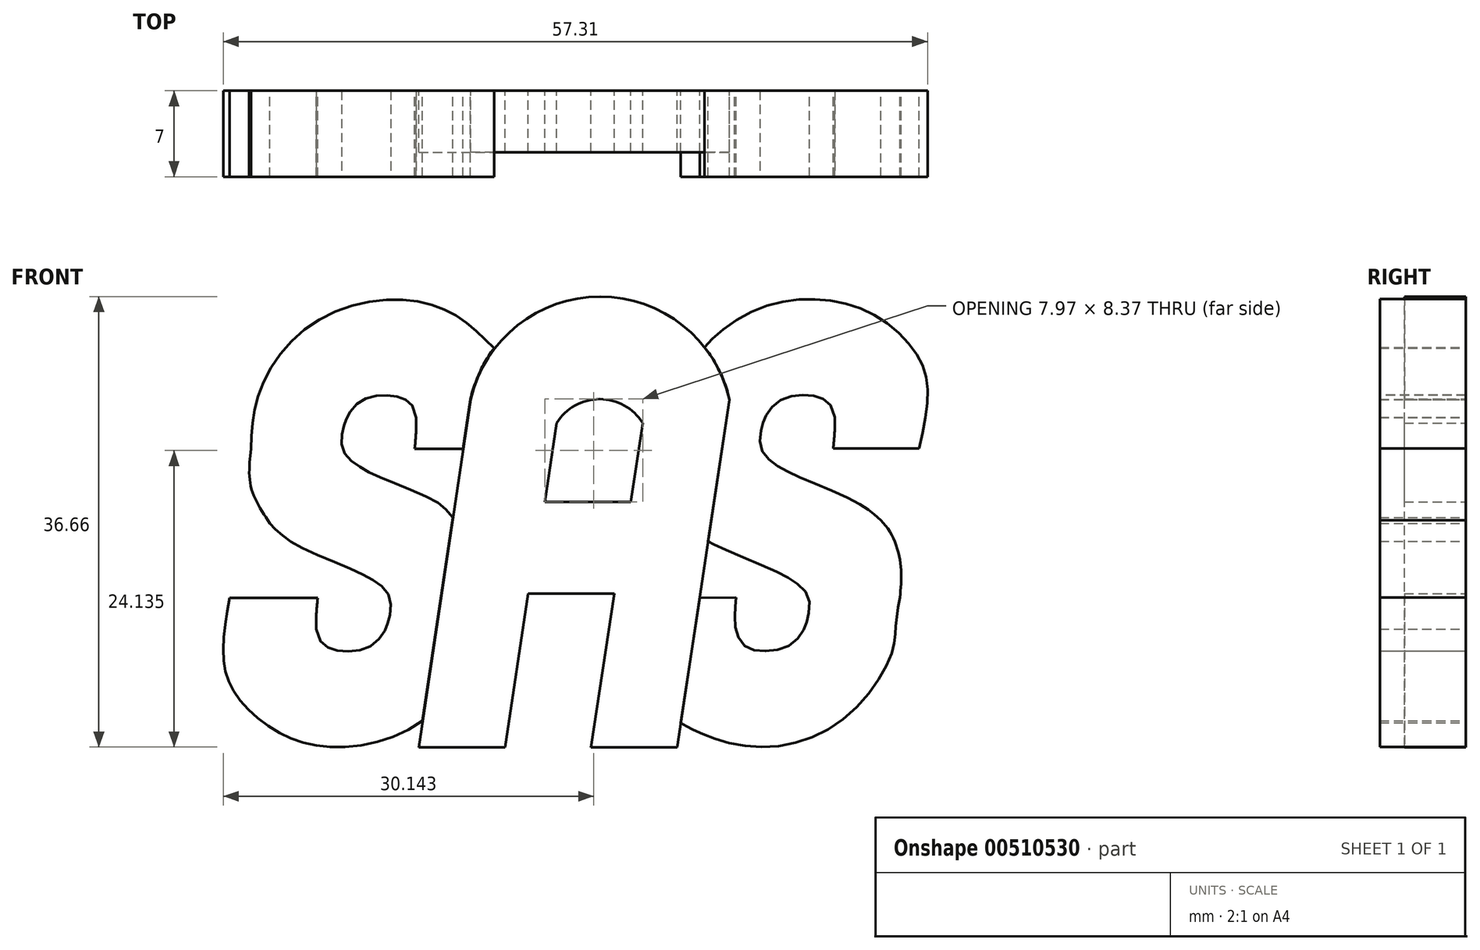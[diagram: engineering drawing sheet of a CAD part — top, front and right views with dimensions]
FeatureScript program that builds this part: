
annotation { "Feature Type Name" : "Feature", "Feature Type Description" : "" }
export const myFeature = defineFeature(function(context is Context, id is Id, definition is map)
    precondition{}
    {
        {
            var Q0;
            Q0=qCreatedBy(makeId("Front.planeOp"),FACE);
            var sketch = newSketch(context, id + "F0", { "sketchPlane" : qUnion([Q0])});
            skLineSegment(sketch, "E0", {"start": v(7, 0) * mm, "end": v(14, 0) * mm});
            skLineSegment(sketch, "E1", {"start": v(28, 0) * mm, "end": v(21, 0) * mm});
            skLineSegment(sketch, "E2", {"start": v(21, 0) * mm, "end": v(22.89, 12.5) * mm});
            skLineSegment(sketch, "E3", {"start": v(22.89, 12.5) * mm, "end": v(15.89, 12.48) * mm});
            skLineSegment(sketch, "E4", {"start": v(15.89, 12.48) * mm, "end": v(14, 0) * mm});
            skLineSegment(sketch, "E5", {"start": v(17.24, 19.95) * mm, "end": v(24.24, 19.95) * mm});
            skLineSegment(sketch, "E6", {"start": v(24.24, 19.95) * mm, "end": v(25.2, 26.38) * mm});
            skLineSegment(sketch, "E7", {"start": v(17.24, 19.95) * mm, "end": v(18.2, 26.38) * mm});
            skLineSegment(sketch, "E8", {"start": v(17.24, 19.95) * mm, "end": v(20.74, 19.95) * mm, "construction": true});
            skPoint(sketch, "E9.endSnap0", {"position": v(21.7, 28.32) * mm});
            skLineSegment(sketch, "E10", {"start": v(28, 0) * mm, "end": v(32.27, 28.28) * mm});
            skLineSegment(sketch, "E11", {"start": v(7, 0) * mm, "end": v(11.21, 28.31) * mm});
            skArc(sketch, "E12", {"start": v(32.27, 28.28) * mm, "mid": v(21.75, 36.66) * mm, "end": v(11.21, 28.31) * mm});
            skArc(sketch, "E13", {"start": v(25.2, 26.38) * mm, "mid": v(21.7, 28.32) * mm, "end": v(18.2, 26.38) * mm});
            skSolve(sketch);
        }
        {
            var Q0;
            Q0=qCreatedBy(makeId("Front.planeOp"),FACE);
            var sketch = newSketch(context, id + "F1", { "sketchPlane" : qUnion([Q0])});
            skLineSegment(sketch, "E14", {"start": v(0, 0) * mm, "end": v(-10.16, 0) * mm, "construction": true});
            skLineSegment(sketch, "E15", {"start": v(0, 0) * mm, "end": v(10.14, 0) * mm, "construction": true});
            skFitSpline(sketch, "E16", {"points": [v(-6.66, 24.28) * mm, v(-6.66, 21.15) * mm, v(-5.12, 18.2) * mm], "startDerivative": vector(-0.75, -6.48) * mm, "endDerivative": vector(3.8, -5.67) * mm});
            skLineSegment(sketch, "E17", {"start": v(6.66, 24.28) * mm, "end": v(0.78, 24.28) * mm, "construction": true});
            skFitSpline(sketch, "E18", {"points": [v(6.78, 26.82) * mm, v(5.8, 28.32) * mm, v(4.13, 28.62) * mm, v(2.18, 28.1) * mm, v(1.14, 26.82) * mm, v(0.84, 25.93) * mm, v(0.78, 24.28) * mm, v(1.93, 22.98) * mm, v(4, 21.9) * mm, v(8.24, 20.05) * mm, v(9.75, 18.67) * mm], "startDerivative": vector(-4.4, 29.75) * mm, "endDerivative": vector(12.93, -18.47) * mm});
            skFitSpline(sketch, "E19", {"points": [v(6.66, 24.28) * mm, v(6.76, 25.47) * mm, v(6.78, 26.82) * mm], "startDerivative": vector(0.34, 3.42) * mm, "endDerivative": vector(-0.13, 3.63) * mm});
            skFitSpline(sketch, "E20.MirrorCS", {"points": [v(-1.36, 9.6) * mm, v(-0.38, 8.09) * mm, v(1.3, 7.8) * mm, v(3.24, 8.32) * mm, v(4.28, 9.6) * mm, v(4.58, 10.49) * mm, v(4.64, 12.14) * mm, v(3.5, 13.44) * mm, v(1.41, 14.52) * mm, v(-2.82, 16.37) * mm, v(-4.28, 17.38) * mm, v(-5.12, 18.2) * mm], "startDerivative": vector(4.4, -29.75) * mm, "endDerivative": vector(-6, 10.66) * mm});
            skFitSpline(sketch, "E21.MirrorCS", {"points": [v(-1.23, 12.14) * mm, v(-1.34, 10.94) * mm, v(-1.36, 9.6) * mm], "startDerivative": vector(-0.34, -3.42) * mm, "endDerivative": vector(0.13, -3.63) * mm});
            skFitSpline(sketch, "E22", {"points": [v(-8.41, 12.14) * mm, v(-8.91, 7.45) * mm, v(-7.96, 4.37) * mm, v(-4.65, 1.34) * mm, v(0.17, 0) * mm, v(7.3, 2.15) * mm], "startDerivative": vector(-4.29, -25.2) * mm, "endDerivative": vector(25.16, 18.75) * mm});
            skLineSegment(sketch, "E23", {"start": v(9.75, 18.67) * mm, "end": v(7.3, 2.15) * mm});
            skLineSegment(sketch, "E24", {"start": v(6.66, 24.28) * mm, "end": v(10.6, 24.27) * mm});
            skFitSpline(sketch, "E25", {"points": [v(-6.66, 24.28) * mm, v(-6.02, 28.74) * mm, v(-1.96, 34.25) * mm, v(5.25, 36.41) * mm, v(10.08, 35.08) * mm, v(13.12, 32.45) * mm], "startDerivative": vector(0.9, 23.94) * mm, "endDerivative": vector(16.5, -16.7) * mm});
            skLineSegment(sketch, "E26", {"start": v(10.6, 24.27) * mm, "end": v(11.2, 28.3) * mm});
            skFitSpline(sketch, "E27", {"points": [v(11.2, 28.3) * mm, v(12, 30.59) * mm, v(13.12, 32.45) * mm], "startDerivative": vector(1.14, 4.85) * mm, "endDerivative": vector(2.8, 3.56) * mm});
            skLineSegment(sketch, "E28", {"start": v(-1.23, 12.14) * mm, "end": v(-8.41, 12.14) * mm});
            skSolve(sketch);
        }
        {
            var Q0;
            Q0=qCreatedBy(makeId("Front.planeOp"),FACE);
            var sketch = newSketch(context, id + "F2", { "sketchPlane" : qUnion([Q0])});
            skLineSegment(sketch, "E29", {"start": v(47.7, 24.3) * mm, "end": v(40.7, 24.3) * mm});
            skFitSpline(sketch, "E30", {"points": [v(40.83, 26.85) * mm, v(39.85, 28.35) * mm, v(38.18, 28.65) * mm, v(36.23, 28.12) * mm, v(35.2, 26.85) * mm, v(34.9, 25.95) * mm, v(34.83, 24.3) * mm, v(35.98, 23) * mm, v(38.06, 21.92) * mm, v(42.3, 20.08) * mm, v(43.8, 19.14) * mm, v(44.58, 18.46) * mm], "startDerivative": vector(-4.4, 29.75) * mm, "endDerivative": vector(15.08, -14.57) * mm});
            skFitSpline(sketch, "E31.MirrorCS", {"points": [v(46.13, 12.17) * mm, v(46.13, 15.29) * mm, v(44.58, 18.46) * mm], "startDerivative": vector(0.75, 6.48) * mm, "endDerivative": vector(-5, 4.63) * mm});
            skFitSpline(sketch, "E32", {"points": [v(40.7, 24.3) * mm, v(40.83, 25.73) * mm, v(40.83, 26.85) * mm], "startDerivative": vector(0.3, 2.77) * mm, "endDerivative": vector(-0.05, 2.32) * mm});
            skLineSegment(sketch, "E33", {"start": v(29.84, 12.14) * mm, "end": v(28.3, 1.98) * mm});
            skLineSegment(sketch, "E34", {"start": v(30.53, 16.75) * mm, "end": v(32.28, 28.28) * mm});
            skFitSpline(sketch, "E35", {"points": [v(32.28, 28.28) * mm, v(31.5, 30.52) * mm, v(30.25, 32.54) * mm], "startDerivative": vector(-1.4, 5.72) * mm, "endDerivative": vector(-2.83, 3.56) * mm});
            skFitSpline(sketch, "E36", {"points": [v(47.7, 24.3) * mm, v(48.39, 29) * mm, v(47.43, 32.07) * mm, v(44.13, 35.1) * mm, v(39.3, 36.44) * mm, v(33.83, 35.3) * mm, v(30.25, 32.54) * mm], "startDerivative": vector(6.21, 28.78) * mm, "endDerivative": vector(-10.58, -13.74) * mm});
            skFitSpline(sketch, "E37", {"points": [v(46.13, 12.17) * mm, v(45.8, 9.86) * mm, v(45.49, 7.7) * mm, v(41.43, 2.2) * mm, v(34.22, 0.03) * mm, v(29.4, 1.36) * mm, v(28.3, 1.98) * mm], "startDerivative": vector(-3.23, -18.4) * mm, "endDerivative": vector(-9.46, 5.8) * mm});
            skFitSpline(sketch, "E38", {"points": [v(30.53, 16.75) * mm, v(31.23, 16.4) * mm, v(35.46, 14.55) * mm, v(37.55, 13.47) * mm, v(38.7, 12.17) * mm, v(38.63, 10.51) * mm, v(38.33, 9.62) * mm, v(37.3, 8.35) * mm, v(35.34, 7.82) * mm, v(33.67, 8.12) * mm, v(32.82, 9.39) * mm, v(32.71, 10.97) * mm, v(32.82, 12.17) * mm], "startDerivative": vector(10.04, -5.38) * mm, "endDerivative": vector(1.15, 17.13) * mm});
            skLineSegment(sketch, "E39", {"start": v(29.84, 12.14) * mm, "end": v(32.82, 12.17) * mm});
            skLineSegment(sketch, "E40", {"start": v(28.3, 1.98) * mm, "end": v(28.34, 1.95) * mm});
            skSolve(sketch);
        }
        {
            var Q0;
            Q0 = qSketchRegion(id + "F0", true);
            extrude(context, id + "F3", {"entities" : qUnion([Q0]), "depth" : 5 * mm});
        }
        {
            var Q0;
            Q0 = qSketchRegion(id + "F1", true);
            extrude(context, id + "F4", {"entities" : qUnion([Q0]), "depth" : 7 * mm});
        }
        {
            var Q0;
            Q0 = qSketchRegion(id + "F2", true);
            extrude(context, id + "F5", {"entities" : qUnion([Q0]), "depth" : 7 * mm});
        }
    });
